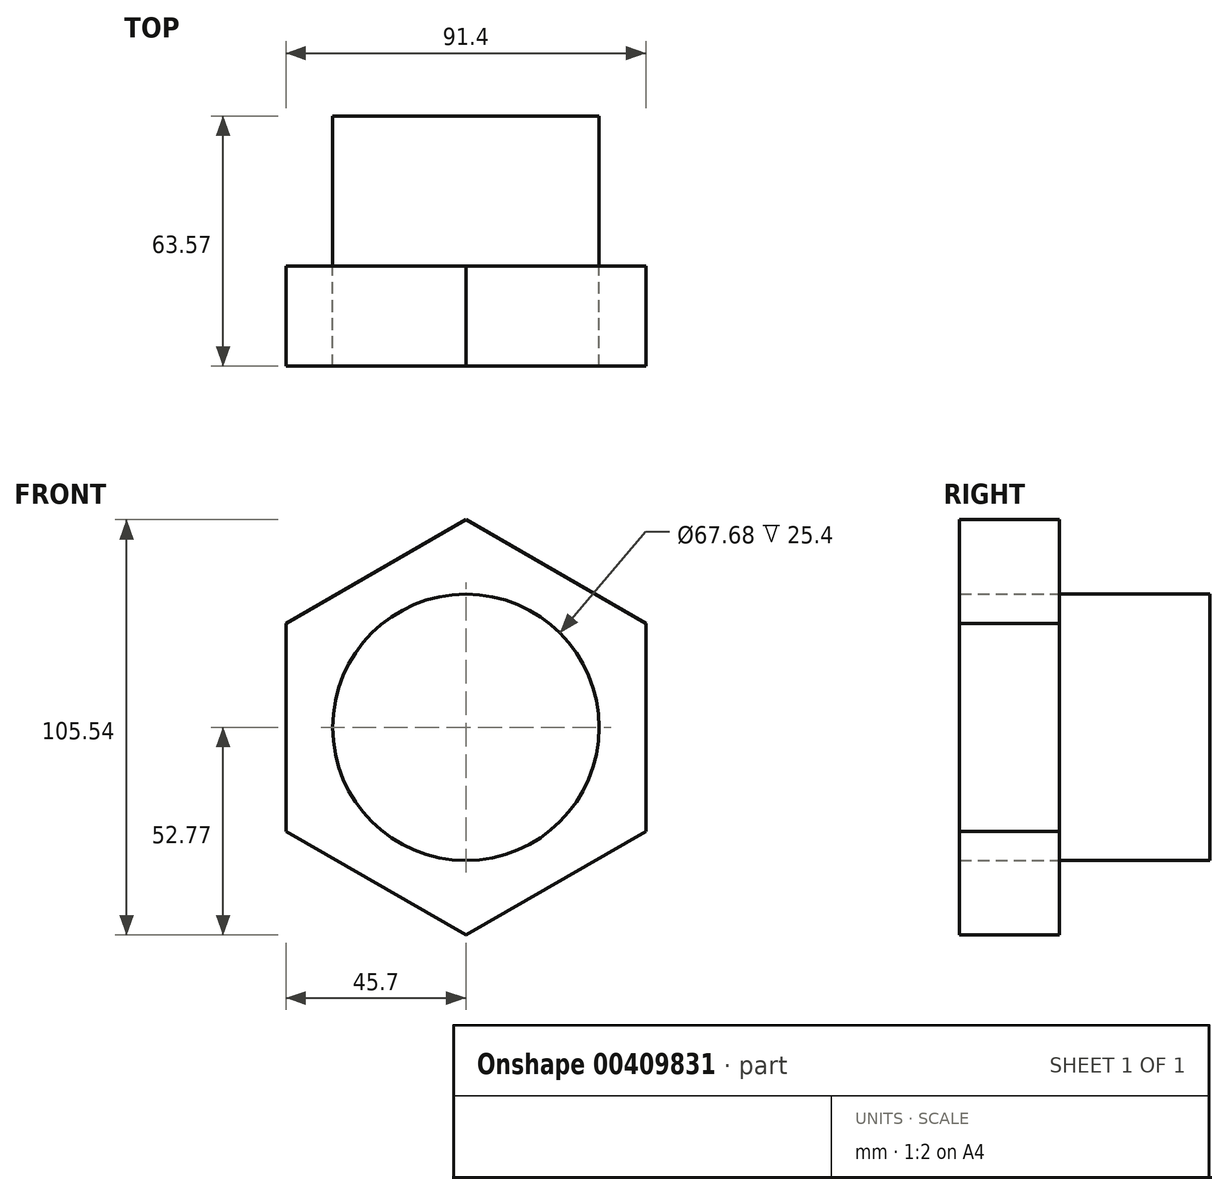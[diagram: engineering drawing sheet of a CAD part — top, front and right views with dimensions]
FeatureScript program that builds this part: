
annotation { "Feature Type Name" : "Feature", "Feature Type Description" : "" }
export const myFeature = defineFeature(function(context is Context, id is Id, definition is map)
    precondition{}
    {
        {
            var Q0;
            Q0=qCreatedBy(makeId("Front.planeOp"),FACE);
            var sketch = newSketch(context, id + "F0", { "sketchPlane" : qUnion([Q0])});
            skLineSegment(sketch, "E0.0", {"start": v(45.7, 26.39) * mm, "end": v(45.7, -26.39) * mm});
            skLineSegment(sketch, "E0.1", {"start": v(45.7, -26.39) * mm, "end": v(0, -52.77) * mm});
            skLineSegment(sketch, "E0.2", {"start": v(0, -52.77) * mm, "end": v(-45.7, -26.39) * mm});
            skLineSegment(sketch, "E0.3", {"start": v(-45.7, -26.39) * mm, "end": v(-45.7, 26.39) * mm});
            skLineSegment(sketch, "E0.4", {"start": v(-45.7, 26.39) * mm, "end": v(0, 52.77) * mm});
            skLineSegment(sketch, "E0.5", {"start": v(0, 52.77) * mm, "end": v(45.7, 26.39) * mm});
            skPoint(sketch, "E0.0.midPoint", {"position": v(45.7, 0) * mm});
            skPoint(sketch, "E0.cCircle.center.orphan", {"position": v(0, 0) * mm});
            skCircle(sketch, "E1", {"center": v(0, 0) * mm, "radius": 33.84 * mm});
            skSolve(sketch);
        }
        {
            var Q0;
            Q0=makeQuery(id+"F0.imprint","IMPRINT",FACE,{"disambiguationData":[TD([[makeQuery(id+"F0.imprint","IMPRINT",EDGE,{"derivedFrom":sQuery(id+"F0.wireOp",EDGE,"E1")}),1.0]])]});
            extrude(context, id + "F1", {"entities" : qUnion([Q0]), "oppositeDirection" : true, "depth" : 38.17 * mm});
        }
        {
            var Q0;
            Q0 = qSketchRegion(id + "F0", true);
            extrude(context, id + "F2", {"entities" : qUnion([Q0]), "depth" : 25.4 * mm});
        }
    });
